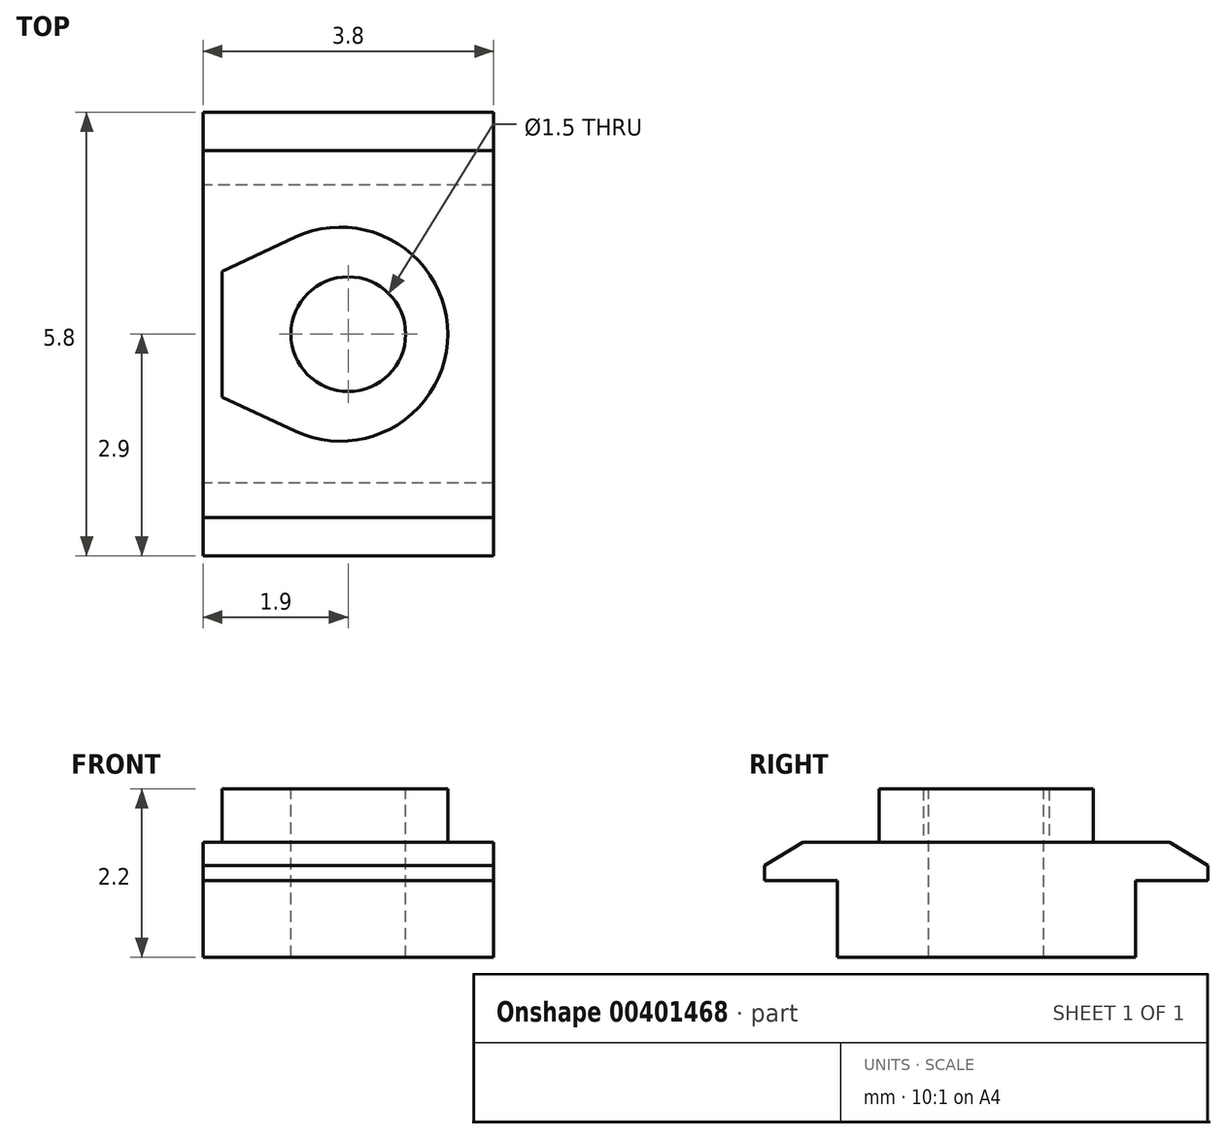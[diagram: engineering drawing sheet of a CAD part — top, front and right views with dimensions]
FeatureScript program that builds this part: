
annotation { "Feature Type Name" : "Feature", "Feature Type Description" : "" }
export const myFeature = defineFeature(function(context is Context, id is Id, definition is map)
    precondition{}
    {
        {
            var Q0;
            Q0=qCreatedBy(makeId("Right.planeOp"),FACE);
            var sketch = newSketch(context, id + "F0", { "sketchPlane" : qUnion([Q0])});
            skLineSegment(sketch, "E0", {"start": v(-2.9, 0) * mm, "end": v(2.9, 0) * mm});
            skLineSegment(sketch, "E1", {"start": v(2.9, 0) * mm, "end": v(2.9, -0.5) * mm});
            skLineSegment(sketch, "E2", {"start": v(2.9, -0.5) * mm, "end": v(1.95, -0.5) * mm});
            skLineSegment(sketch, "E3", {"start": v(1.95, -0.5) * mm, "end": v(1.95, -1.5) * mm});
            skLineSegment(sketch, "E4", {"start": v(1.95, -1.5) * mm, "end": v(-1.95, -1.5) * mm});
            skLineSegment(sketch, "E5", {"start": v(-1.95, -1.5) * mm, "end": v(-1.95, -0.5) * mm});
            skLineSegment(sketch, "E6", {"start": v(-1.95, -0.5) * mm, "end": v(-2.9, -0.5) * mm});
            skLineSegment(sketch, "E7", {"start": v(-2.9, -0.5) * mm, "end": v(-2.9, 0) * mm});
            skLineSegment(sketch, "E8", {"start": v(0, -1.5) * mm, "end": v(0, 0) * mm, "construction": true});
            skSolve(sketch);
        }
        {
            var Q0;
            Q0 = qSketchRegion(id + "F0", true);
            extrude(context, id + "F1", {"entities" : qUnion([Q0]), "endBound" : BoundingType.SYMMETRIC, "depth" : 3.8 * mm});
        }
        {
            var Q0;
            Q0=makeQuery(id+"F1.opExtrude","SWEPT_EDGE",EDGE,{"disambiguationData":[OSD([sQuery(id+"F0.wireOp",EDGE,"E0"),sQuery(id+"F0.wireOp",EDGE,"E1")])]});
            chamfer(context, id + "F2", {"entities" : qUnion([Q0]), "chamferType" : ChamferType.TWO_OFFSETS, "width1" : 0.3 * mm, "oppositeDirection" : true, "width2" : 0.5 * mm, "tangentPropagation" : true});
        }
        {
            var Q0;
            Q0=makeQuery(id+"F1.opExtrude","SWEPT_EDGE",EDGE,{"disambiguationData":[OSD([sQuery(id+"F0.wireOp",EDGE,"E0"),sQuery(id+"F0.wireOp",EDGE,"E7")])]});
            chamfer(context, id + "F3", {"entities" : qUnion([Q0]), "chamferType" : ChamferType.TWO_OFFSETS, "width1" : 0.3 * mm, "oppositeDirection" : false, "width2" : 0.5 * mm, "tangentPropagation" : true});
        }
        {
            var Q0;
            Q0=makeQuery(id+"F1.opExtrude","SWEPT_FACE",FACE,{"disambiguationData":[OSD([sQuery(id+"F0.wireOp",EDGE,"E0")])]});
            var sketch = newSketch(context, id + "F4", { "sketchPlane" : qUnion([Q0])});
            skArc(sketch, "E9", {"start": v(-0.7, -1.27) * mm, "mid": v(1.3, 0) * mm, "end": v(-0.7, 1.27) * mm});
            skLineSegment(sketch, "E10", {"start": v(-0.7, 1.27) * mm, "end": v(-1.65, 0.82) * mm});
            skLineSegment(sketch, "E11", {"start": v(-1.65, 0.82) * mm, "end": v(-1.65, -0.82) * mm});
            skLineSegment(sketch, "E12", {"start": v(-1.65, -0.82) * mm, "end": v(-0.7, -1.27) * mm});
            skSolve(sketch);
        }
        {
            var Q0;
            Q0 = qSketchRegion(id + "F4", true);
            extrude(context, id + "F5", {"entities" : qUnion([Q0]), "operationType" : NewBodyOperationType.ADD, "depth" : 0.7 * mm});
        }
        {
            var Q0;
            Q0=makeQuery(id+"F5.opExtrude","CAP_FACE",FACE,{"disambiguationData":[OSD([sQuery(id+"F4.wireOp",EDGE,"E9"),sQuery(id+"F4.wireOp",EDGE,"E10"),sQuery(id+"F4.wireOp",EDGE,"E11"),sQuery(id+"F4.wireOp",EDGE,"E12")])],"isStart":false});
            var sketch = newSketch(context, id + "F6", { "sketchPlane" : qUnion([Q0])});
            skCircle(sketch, "E13", {"center": v(0, 0) * mm, "radius": 0.75 * mm});
            skSolve(sketch);
        }
        {
            var Q0;
            Q0 = qSketchRegion(id + "F6", true);
            extrude(context, id + "F7", {"entities" : qUnion([Q0]), "operationType" : NewBodyOperationType.REMOVE, "endBound" : BoundingType.UP_TO_NEXT, "oppositeDirection" : true, "depth" : 25 * mm});
        }
    });
